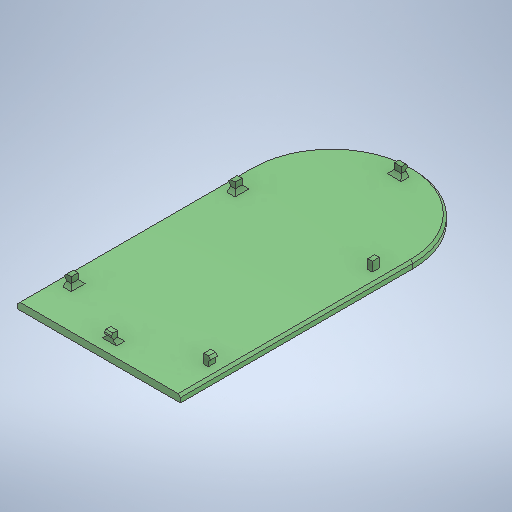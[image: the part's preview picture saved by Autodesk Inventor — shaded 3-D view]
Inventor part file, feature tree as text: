
AUTODESK INVENTOR PART (.ipt)
format: ipt  version: 2025.2 (Build 292293000, 293)  size: 381,952 bytes
history: native  units: mm
features: sketch x6, extrude x5, chamfer x2, sweep x1, plane x1, fillet x1, mirror x1, projected_geometry x1
ambient origin geometry x8: Origin, YZ Plane, XZ Plane, XY Plane, X Axis, Y Axis, Z Axis, Center Point
bodies: Solid1 (feature_tree)
feature tree (18):
  extrude  "Extrusion1"  Depth=70.0mm
  extrude  "Extrusion2"  Depth=4.5mm
  sketch  "Sketch4"  dims[d15=2.0mm d16=3.0mm]
  extrude  "Extrusion3"  Depth=3.0mm
  extrude  "Extrusion4"  Depth=3.0mm
  extrude  "Extrusion5"  Depth=2.0mm
  sweep  "Sweep1"
  plane  "Work Plane1"
  chamfer  "Chamfer1"  [1 undecoded]
  fillet  "Fillet1"  Radius=10.0mm
  mirror  "Mirror1"
  chamfer  "Chamfer2"  Distance=1.0mm
  sketch  "Sketch1"  dims[d0=70.0mm d1=100.0mm]
  sketch  "Sketch3"  dims[d2=3.0mm d3=0.0mm d14=4.5mm]
  projected_geometry  "Projected Loop1"
  sketch  "Sketch5"  dims[d17=10.0mm d18=3.0mm]
  sketch  "Sketch6"  dims[d19=4.0mm d20=0.0mm d21=1.0mm d22=45.0deg d23=0.0mm d24=0.0mm d25=10.0mm d26=0.0mm d27=1.0mm d28=45.0deg d29=10.0mm d30=0.0mm d31=45.0deg d33=1.0mm d34=0.0mm d35=0.0mm d36=1.5mm d37=2.0mm d38=45.0deg d39=0.5mm d40=1.0mm d41=2.0mm d42=45.0deg]
  sketch  "3D Sketch1"
note: 1 required parameter value undecoded (feature->parameter linkage not recoverable at this tier; creation-order binding heuristic only, values carry confidence <= 0.55)
